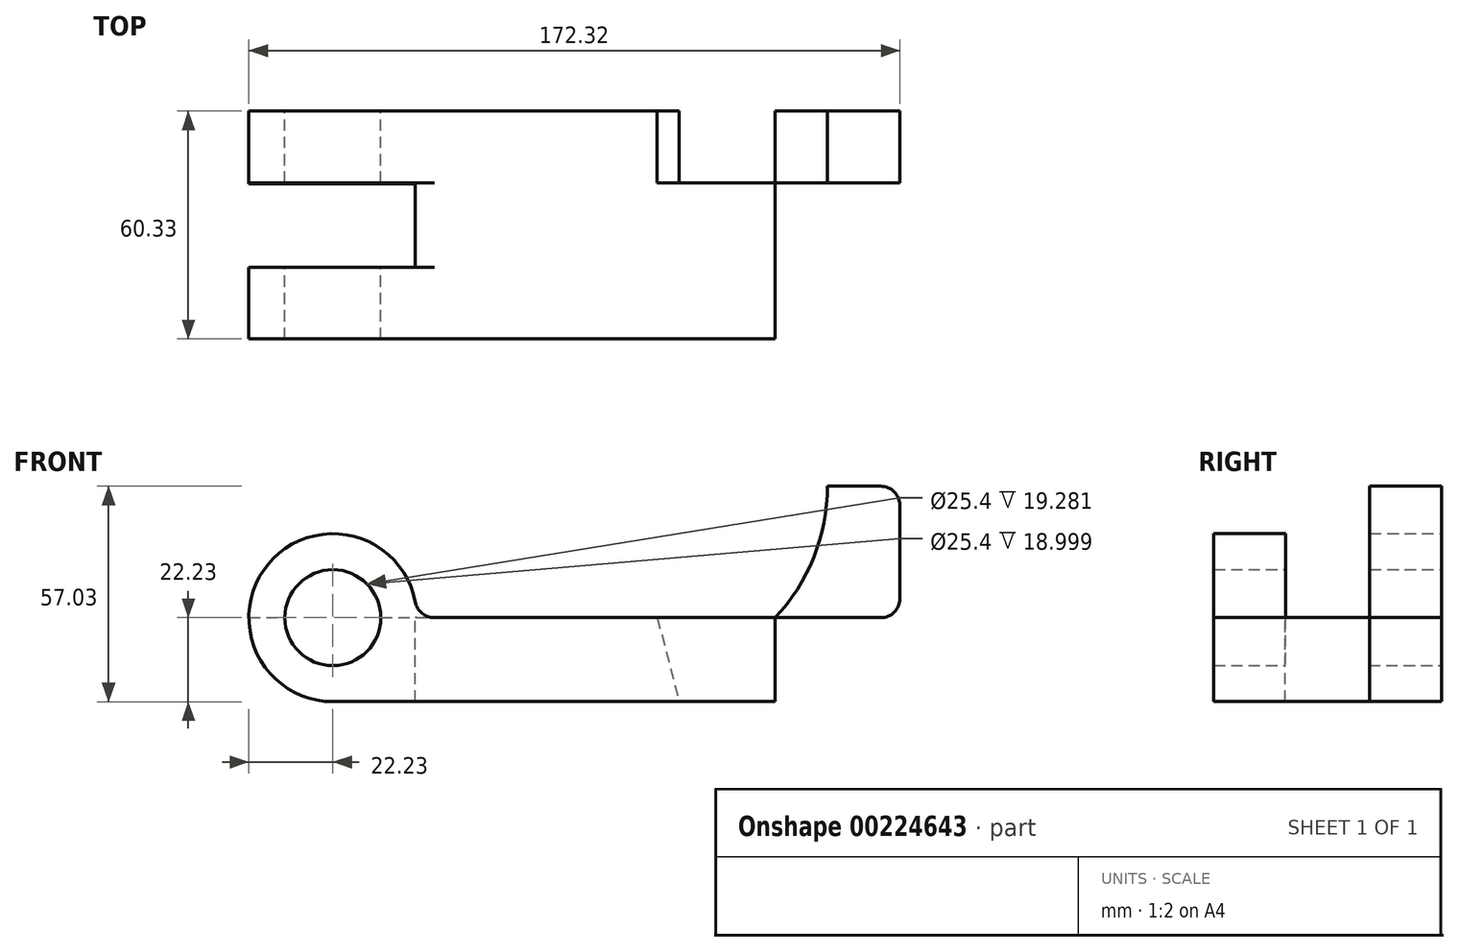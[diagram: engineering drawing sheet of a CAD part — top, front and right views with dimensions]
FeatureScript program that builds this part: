
annotation { "Feature Type Name" : "Feature", "Feature Type Description" : "" }
export const myFeature = defineFeature(function(context is Context, id is Id, definition is map)
    precondition{}
    {
        {
            var Q0;
            Q0=qCreatedBy(makeId("Front.planeOp"),FACE);
            var sketch = newSketch(context, id + "F0", { "sketchPlane" : qUnion([Q0])});
            skCircle(sketch, "E0", {"center": v(0, 0) * mm, "radius": 12.7 * mm});
            skCircle(sketch, "E1", {"center": v(0, 0) * mm, "radius": 22.23 * mm});
            skLineSegment(sketch, "E2", {"start": v(0, -22.23) * mm, "end": v(194.2, -22.23) * mm});
            skLineSegment(sketch, "E3", {"start": v(22.22, 0) * mm, "end": v(194.2, 0) * mm});
            skLineSegment(sketch, "E4", {"start": v(194.2, 0) * mm, "end": v(194.2, -22.23) * mm});
            skLineSegment(sketch, "E5", {"start": v(0, 0) * mm, "end": v(85.85, 0) * mm});
            skLineSegment(sketch, "E6", {"start": v(0, -22.23) * mm, "end": v(91.7, -22.23) * mm});
            skLineSegment(sketch, "E7", {"start": v(85.85, 0) * mm, "end": v(91.7, -22.23) * mm});
            skLineSegment(sketch, "E8", {"start": v(0, -22.23) * mm, "end": v(117.1, -22.23) * mm});
            skLineSegment(sketch, "E9", {"start": v(117.1, -22.23) * mm, "end": v(117.1, 0) * mm});
            skLineSegment(sketch, "E10", {"start": v(150.09, 34.8) * mm, "end": v(150.09, 0) * mm});
            skLineSegment(sketch, "E11", {"start": v(130.88, 34.8) * mm, "end": v(130.88, 0) * mm});
            skLineSegment(sketch, "E12", {"start": v(130.88, 34.8) * mm, "end": v(150.09, 34.8) * mm});
            skArc(sketch, "E13", {"start": v(117.1, 0) * mm, "mid": v(127.31, 16.08) * mm, "end": v(130.88, 34.8) * mm});
            skSolve(sketch);
        }
        {
            var Q0;
            {var subQ5=sQuery(id+"F0.wireOp",EDGE,"E7");Q0=makeQuery(id+"F0.imprint","IMPRINT",FACE,{"disambiguationData":[TD([[makeQuery(id+"F0.imprint","IMPRINT",EDGE,{"derivedFrom":subQ5}),-1.0]])]});}
            var Q1;
            Q1=makeQuery(id+"F0.imprint","IMPRINT",FACE,{"disambiguationData":[TD([[makeQuery(id+"F0.imprint","IMPRINT",EDGE,{"derivedFrom":sQuery(id+"F0.wireOp",EDGE,"E0")}),-1.0]])]});
            var Q2;
            Q2=makeQuery(id+"F0.imprint","IMPRINT",FACE,{"disambiguationData":[TD([[makeQuery(id+"F0.imprint","IMPRINT",EDGE,{"derivedFrom":sQuery(id+"F0.wireOp",EDGE,"E2")}),1.0]])]});
            var Q3;
            {var subQ0=sQuery(id+"F0.wireOp",EDGE,"E7");Q3=makeQuery(id+"F0.imprint","IMPRINT",FACE,{"disambiguationData":[TD([[makeQuery(id+"F0.imprint","IMPRINT",EDGE,{"derivedFrom":subQ0}),1.0]])]});}
            var Q4;
            {var subQ2=sQuery(id+"F0.wireOp",EDGE,"E11");Q4=makeQuery(id+"F0.imprint","IMPRINT",FACE,{"disambiguationData":[TD([[makeQuery(id+"F0.imprint","IMPRINT",EDGE,{"derivedFrom":subQ2}),-1.0]])]});}
            var Q5;
            {var subQ0=sQuery(id+"F0.wireOp",EDGE,"E10");Q5=makeQuery(id+"F0.imprint","IMPRINT",FACE,{"disambiguationData":[TD([[makeQuery(id+"F0.imprint","IMPRINT",EDGE,{"derivedFrom":subQ0}),-1.0]])]});}
            extrude(context, id + "F1", {"entities" : qUnion([Q0, Q1, Q2, Q3, Q4, Q5]), "depth" : 60.32 * mm});
        }
        {
            var Q0;
            Q0=qCreatedBy(makeId("Top.planeOp"),FACE);
            var sketch = newSketch(context, id + "F2", { "sketchPlane" : qUnion([Q0])});
            skLineSegment(sketch, "E14", {"start": v(-26.84, -19) * mm, "end": v(27.32, -19) * mm});
            skLineSegment(sketch, "E15", {"start": v(27.32, -19) * mm, "end": v(27.32, -41.33) * mm});
            skLineSegment(sketch, "E16", {"start": v(27.32, -41.33) * mm, "end": v(-26.84, -41.33) * mm});
            skLineSegment(sketch, "E17", {"start": v(-26.84, -41.33) * mm, "end": v(-26.84, -19) * mm});
            skSolve(sketch);
        }
        {
            var Q0;
            Q0=makeQuery(id+"F2.imprint","IMPRINT",FACE,{"disambiguationData":[TD([[makeQuery(id+"F2.imprint","IMPRINT",EDGE,{"derivedFrom":sQuery(id+"F2.wireOp",EDGE,"E14")}),-1.0]])]});
            extrude(context, id + "F3", {"entities" : qUnion([Q0]), "operationType" : NewBodyOperationType.REMOVE, "endBound" : BoundingType.THROUGH_ALL, "depth" : 50.8 * mm});
        }
        {
            var Q0;
            Q0=qCreatedBy(makeId("Top.planeOp"),FACE);
            var sketch = newSketch(context, id + "F4", { "sketchPlane" : qUnion([Q0])});
            skLineSegment(sketch, "E18", {"start": v(-22.28, -19.28) * mm, "end": v(21.83, -19.28) * mm});
            skLineSegment(sketch, "E19", {"start": v(21.83, -19.28) * mm, "end": v(21.83, -41.45) * mm});
            skLineSegment(sketch, "E20", {"start": v(21.83, -41.45) * mm, "end": v(-22.28, -41.45) * mm});
            skLineSegment(sketch, "E21", {"start": v(-22.28, -41.45) * mm, "end": v(-22.28, -19.28) * mm});
            skSolve(sketch);
        }
        {
            var Q0;
            Q0=makeQuery(id+"F4.imprint","IMPRINT",FACE,{"disambiguationData":[TD([[makeQuery(id+"F4.imprint","IMPRINT",EDGE,{"derivedFrom":sQuery(id+"F4.wireOp",EDGE,"E18")}),-1.0]])]});
            extrude(context, id + "F5", {"entities" : qUnion([Q0]), "operationType" : NewBodyOperationType.REMOVE, "oppositeDirection" : true, "depth" : 25.4 * mm});
        }
        {
            var Q0;
            {var subQ0=sQuery(id+"F0.wireOp",EDGE,"E7");Q0=makeQuery(id+"F0.imprint","IMPRINT",FACE,{"disambiguationData":[TD([[makeQuery(id+"F0.imprint","IMPRINT",EDGE,{"derivedFrom":subQ0}),1.0]])]});}
            extrude(context, id + "F6", {"entities" : qUnion([Q0]), "operationType" : NewBodyOperationType.REMOVE, "oppositeDirection" : true, "depth" : 19.05 * mm});
        }
        {
            var Q0;
            {var subQ0=sQuery(id+"F0.wireOp",EDGE,"E7");Q0=makeQuery(id+"F0.imprint","IMPRINT",FACE,{"disambiguationData":[TD([[makeQuery(id+"F0.imprint","IMPRINT",EDGE,{"derivedFrom":subQ0}),1.0]])]});}
            extrude(context, id + "F7", {"entities" : qUnion([Q0]), "operationType" : NewBodyOperationType.REMOVE, "depth" : 19.05 * mm});
        }
        {
            var Q0;
            Q0=makeQuery(id+"F1.opExtrude","SWEPT_FACE",FACE,{"disambiguationData":[OSD([sQuery(id+"F0.wireOp",EDGE,"E10")])]});
            var sketch = newSketch(context, id + "F8", { "sketchPlane" : qUnion([Q0])});
            skLineSegment(sketch, "E22", {"start": v(0, 0) * mm, "end": v(-19.05, 0) * mm});
            skLineSegment(sketch, "E23", {"start": v(-19.05, 0) * mm, "end": v(-19.05, 34.8) * mm});
            skLineSegment(sketch, "E24", {"start": v(-19.05, 34.8) * mm, "end": v(0, 34.8) * mm});
            skLineSegment(sketch, "E25", {"start": v(0, 34.8) * mm, "end": v(0, 0) * mm});
            skSolve(sketch);
        }
        {
            var Q0;
            {var subQ0=sQuery(id+"F8.wireOp",EDGE,"E23");Q0=makeQuery(id+"F8.imprint","IMPRINT",FACE,{"disambiguationData":[TD([[makeQuery(id+"F8.imprint","IMPRINT",EDGE,{"derivedFrom":subQ0}),1.0]])]});}
            extrude(context, id + "F9", {"entities" : qUnion([Q0]), "operationType" : NewBodyOperationType.REMOVE, "oppositeDirection" : true, "depth" : 50.8 * mm});
        }
        {
            var Q0;
            {var subQ0=sQuery(id+"F0.wireOp",EDGE,"E3");Q0=makeQuery(id+"F9.boolean.opBoolean","MERGE",FACE,{"derivedFrom":[makeQuery(id+"F1.opExtrude","SWEPT_FACE",FACE,{"disambiguationData":[OSD([subQ0])]}),makeQuery(id+"F3.boolean.opBoolean","MERGE",FACE,{"derivedFrom":[makeQuery(id+"F1.opExtrude","SWEPT_FACE",FACE,{"disambiguationData":[OSD([subQ0,sQuery(id+"F0.wireOp",EDGE,"E5")])]}),makeQuery(id+"F3.opExtrude","CAP_FACE",FACE,{"disambiguationData":[OSD([sQuery(id+"F2.wireOp",EDGE,"E14"),sQuery(id+"F2.wireOp",EDGE,"E15"),sQuery(id+"F2.wireOp",EDGE,"E16"),sQuery(id+"F2.wireOp",EDGE,"E17")])],"isStart":true})]}),makeQuery(id+"F9.opExtrude","SWEPT_FACE",FACE,{"disambiguationData":[OSD([subQ0,sQuery(id+"F0.wireOp",EDGE,"E10")])]})]});}
            var sketch = newSketch(context, id + "F10", { "sketchPlane" : qUnion([Q0])});
            skCircle(sketch, "E26", {"center": v(155.35, -31.62) * mm, "radius": 6.35 * mm});
            skSolve(sketch);
        }
        {
            var Q0;
            Q0=makeQuery(id+"F10.imprint","IMPRINT",FACE,{"disambiguationData":[TD([[makeQuery(id+"F10.imprint","IMPRINT",EDGE,{"derivedFrom":sQuery(id+"F10.wireOp",EDGE,"E26")}),1.0]])]});
            var Q1;
            Q1=sQuery(id+"F10.wireOp",EDGE,"E26");
            extrude(context, id + "F11", {"entities" : qUnion([Q0]), "operationType" : NewBodyOperationType.REMOVE, "surfaceEntities" : qUnion([Q1]), "endBound" : BoundingType.THROUGH_ALL, "oppositeDirection" : true, "depth" : 25.4 * mm});
        }
        {
            var Q0;
            Q0=makeQuery(id+"F1.opExtrude","SWEPT_EDGE",EDGE,{"disambiguationData":[OSD([sQuery(id+"F0.wireOp",EDGE,"E10"),sQuery(id+"F0.wireOp",EDGE,"E12")])]});
            var Q1;
            Q1=makeQuery(id+"F1.opExtrude","SWEPT_EDGE",EDGE,{"disambiguationData":[OSD([sQuery(id+"F0.wireOp",EDGE,"E3"),sQuery(id+"F0.wireOp",EDGE,"E10")])]});
            var Q2;
            Q2=makeQuery(id+"F1.opExtrude","SWEPT_EDGE",EDGE,{"disambiguationData":[OSD([sQuery(id+"F0.wireOp",EDGE,"E3"),sQuery(id+"F0.wireOp",EDGE,"E4")])]});
            var Q3;
            {var subQ0=sQuery(id+"F2.wireOp",EDGE,"E16");var subQ1=sQuery(id+"F0.wireOp",EDGE,"E5");var subQ3=sQuery(id+"F0.wireOp",EDGE,"E1");Q3=makeQuery(id+"F3.boolean.opBoolean","SPLIT",EDGE,{"disambiguationData":[TD([makeQuery(id+"F3.opExtrude","SWEPT_FACE",FACE,{"disambiguationData":[OSD([subQ0])]})])],"derivedFrom":makeQuery(id+"F1.opExtrude","SWEPT_EDGE",EDGE,{"disambiguationData":[OSD([subQ3,subQ1])]})});}
            var Q4;
            {var subQ0=sQuery(id+"F0.wireOp",EDGE,"E5");var subQ2=sQuery(id+"F2.wireOp",EDGE,"E14");var subQ3=sQuery(id+"F0.wireOp",EDGE,"E1");Q4=makeQuery(id+"F3.boolean.opBoolean","SPLIT",EDGE,{"disambiguationData":[TD([makeQuery(id+"F3.opExtrude","SWEPT_FACE",FACE,{"disambiguationData":[OSD([subQ2])]})])],"derivedFrom":makeQuery(id+"F1.opExtrude","SWEPT_EDGE",EDGE,{"disambiguationData":[OSD([subQ3,subQ0])]})});}
            fillet(context, id + "F12", {"entities" : qUnion([Q0, Q1, Q2, Q3, Q4]), "radius" : 5.08 * mm, "tangentPropagation" : true, "allowEdgeOverflow" : false});
        }
    });
